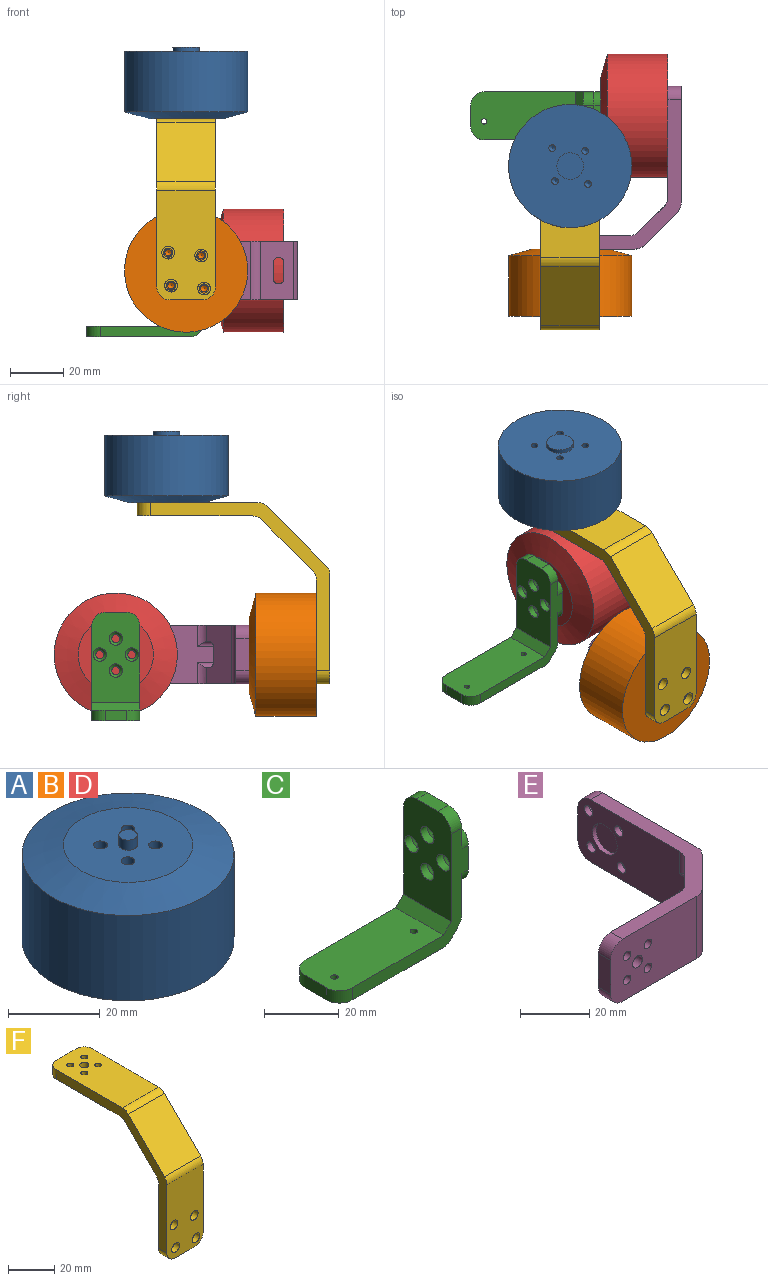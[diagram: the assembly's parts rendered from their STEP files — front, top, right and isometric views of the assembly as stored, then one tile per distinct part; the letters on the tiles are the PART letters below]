
ASSEMBLY  parts=6 mates=5
PART A: 24 faces, bbox 46.2x46.2x29.5 mm
  f0: cylinder r=23.1mm len=46.2mm, axis (0,0,-1), area 3302mm2, adj f2,f21
  f1: plane 28.2x28.2mm, normal (0,0,1), area 583.7mm2, adj f4,f6,f8,f10,f19,f21
  f2: plane 46.2x46.2mm, normal (0,0,-1), area 1578.2mm2, adj f0,f12,f14,f16,f18,f22
  f3: cone r=0mm half-angle=59deg, axis (0,0,1), area 8.2mm2, adj f4
  f4: cylinder r=1.5mm len=7mm, axis (0,0,1), area 66mm2, adj f1,f3
  f5: cone r=0mm half-angle=59deg, axis (0,0,1), area 8.2mm2, adj f6
  f6: cylinder r=1.5mm len=7mm, axis (0,0,1), area 66mm2, adj f1,f5
  f7: cone r=0mm half-angle=59deg, axis (0,0,1), area 8.2mm2, adj f8
  f8: cylinder r=1.5mm len=7mm, axis (0,0,1), area 66mm2, adj f1,f7
  f9: cone r=0mm half-angle=59deg, axis (0,0,1), area 8.2mm2, adj f10
  f10: cylinder r=1.5mm len=7mm, axis (0,0,1), area 66mm2, adj f1,f9
  f11: cone r=0mm half-angle=59deg, axis (0,0,-1), area 5.7mm2, adj f12
  f12: cylinder r=1.25mm len=7mm, axis (0,0,-1), area 55mm2, adj f2,f11
  f13: cone r=0mm half-angle=59deg, axis (0,0,-1), area 5.7mm2, adj f14
  f14: cylinder r=1.25mm len=7mm, axis (0,0,-1), area 55mm2, adj f2,f13
  f15: cone r=0mm half-angle=59deg, axis (0,0,-1), area 5.7mm2, adj f16
  f16: cylinder r=1.25mm len=7mm, axis (0,0,-1), area 55mm2, adj f2,f15
  f17: cone r=0mm half-angle=59deg, axis (0,0,-1), area 5.7mm2, adj f18
  f18: cylinder r=1.25mm len=7mm, axis (0,0,-1), area 55mm2, adj f2,f17
  f19: cylinder r=2mm len=4mm, axis (0,0,-1), area 33.9mm2, adj f1,f20
  f20: plane 4x4mm, normal (0,0,1), area 12.6mm2, adj f19
  f21: cone r=14.1mm half-angle=74.5deg, axis (0,0,-1), area 1091.6mm2, adj f0,f1
  f22: cylinder r=5mm len=10mm, axis (0,0,1), area 47.1mm2, adj f2,f23
  f23: plane 10x10mm, normal (0,0,-1), area 78.5mm2, adj f22
PART B: same geometry as A
PART C: 48 faces, bbox 48.7x18x40.6 mm
  f0: plane 18x11.82mm, normal (1,0,0), area 122.8mm2, adj f7,f9,f10,f11,f38,f41,f44,f46
  f1: plane 18x2.97mm, normal (-0.71,0,0.71), area 75.6mm2, adj f2,f8,f9,f10
  f2: plane 39.26x18mm, normal (0,0,1), area 689.6mm2, adj f1,f3,f9,f10,f14,f17,f45,f47
  f3: plane 8x4mm, normal (-1,0,0), area 32mm2, adj f2,f4,f45,f47
  f4: plane 38.84x18mm, normal (0,0,-1), area 653.8mm2, adj f3,f9,f10,f16,f19,f35,f37,f42
  f5: plane 18x2.38mm, normal (0.71,0,-0.71), area 60.7mm2, adj f9,f10,f42,f43
  f6: plane 18x13.42mm, normal (1,0,0), area 162.2mm2, adj f9,f10,f12,f39,f40,f43
  f7: plane 8x4mm, normal (0,0,1), area 32mm2, adj f0,f8,f44,f46
  f8: plane 33.65x18mm, normal (-1,0,0), area 516.4mm2, adj f1,f7,f9,f10,f21,f23,f25,f27
  f9: plane 43.73x35.62mm, normal (0,1,0), area 300.6mm2, adj f0,f1,f2,f4,f5,f6,f8,f13
  f10: plane 43.73x35.62mm, normal (0,-1,0), area 300.6mm2, adj f0,f1,f2,f4,f5,f6,f8,f13
  f11: plane 8x2.5mm, normal (0,0,1), area 20mm2, adj f0,f13,f38,f41
  f12: plane 8x2.5mm, normal (0,0,-1), area 20mm2, adj f6,f13,f39,f40
  f13: plane 18x18mm, normal (1,0,0), area 261.7mm2, adj f9,f10,f11,f12,f20,f22,f24,f26
  f14: cylinder r=1mm len=2mm, axis (0,0,-1), area 12.6mm2, adj f2,f15
  f15: plane 4x4mm, normal (0,0,-1), area 9.4mm2, adj f14,f16
  f16: cylinder r=2mm len=4mm, axis (0,0,-1), area 25.1mm2, adj f4,f15
  f17: cylinder r=1mm len=2mm, axis (0,0,-1), area 12.6mm2, adj f2,f18
  f18: plane 4x4mm, normal (0,0,-1), area 9.4mm2, adj f17,f19
  f19: cylinder r=2mm len=4mm, axis (0,0,-1), area 25.1mm2, adj f4,f18
  f20: cylinder r=1.5mm len=3mm, axis (-1,0,0), area 28.3mm2, adj f13,f29
  f21: cylinder r=2.5mm len=5mm, axis (-1,0,0), area 39.3mm2, adj f8,f29
  f22: cylinder r=1.5mm len=3mm, axis (-1,0,0), area 28.3mm2, adj f13,f28
  f23: cylinder r=2.5mm len=5mm, axis (-1,0,0), area 39.3mm2, adj f8,f28
  f24: cylinder r=1.5mm len=3mm, axis (-1,0,0), area 28.3mm2, adj f13,f30
  f25: cylinder r=2.5mm len=5mm, axis (-1,0,0), area 39.3mm2, adj f8,f30
  f26: cylinder r=1.5mm len=3mm, axis (-1,0,0), area 28.3mm2, adj f13,f31
  f27: cylinder r=2.5mm len=5mm, axis (-1,0,0), area 39.3mm2, adj f8,f31
  f28: cone r=1.5mm half-angle=45deg, axis (-1,0,0), area 17.8mm2, adj f22,f23
  f29: cone r=1.5mm half-angle=45deg, axis (-1,0,0), area 17.8mm2, adj f20,f21
  f30: cone r=1.5mm half-angle=45deg, axis (-1,0,0), area 17.8mm2, adj f24,f25
  f31: cone r=1.5mm half-angle=45deg, axis (-1,0,0), area 17.8mm2, adj f26,f27
  f32: cylinder r=2mm len=4mm, axis (1,0,0), area 37.7mm2, adj f13,f33
  f33: plane 4x4mm, normal (1,0,0), area 12.6mm2, adj f32
  f34: cone r=0mm half-angle=59deg, axis (0,0,-1), area 5.5mm2, adj f35
  f35: cylinder r=1.22mm len=2.5mm, axis (0,0,-1), area 19.2mm2, adj f4,f34
  f36: cone r=0mm half-angle=59deg, axis (0,0,-1), area 5.5mm2, adj f37
  f37: cylinder r=1.22mm len=2.5mm, axis (0,0,-1), area 19.2mm2, adj f4,f36
  f38: cylinder r=5mm len=5mm, axis (1,0,0), area 19.6mm2, adj f0,f9,f11,f13
  f39: cylinder r=5mm len=5mm, axis (-1,0,0), area 19.6mm2, adj f6,f9,f12,f13
  f40: cylinder r=5mm len=5mm, axis (1,0,0), area 19.6mm2, adj f6,f10,f12,f13
  f41: cylinder r=5mm len=5mm, axis (-1,0,0), area 19.6mm2, adj f0,f10,f11,f13
  f42: cylinder r=5mm len=18mm, axis (0,-1,0), area 70.7mm2, adj f4,f5,f9,f10
  f43: cylinder r=5mm len=18mm, axis (0,-1,0), area 70.7mm2, adj f5,f6,f9,f10
  f44: cylinder r=5mm len=5mm, axis (-1,0,0), area 31.4mm2, adj f0,f7,f8,f10
  f45: cylinder r=5mm len=5mm, axis (0,0,-1), area 31.4mm2, adj f2,f3,f4,f10
  f46: cylinder r=5mm len=5mm, axis (1,0,0), area 31.4mm2, adj f0,f7,f8,f9
  f47: cylinder r=5mm len=5mm, axis (0,0,1), area 31.4mm2, adj f2,f3,f4,f9
PART D: same geometry as A
PART E: 50 faces, bbox 52.7x61x22 mm
  f0: plane 33.23x22mm, normal (0,1,0), area 641.7mm2, adj f1,f8,f9,f23,f25,f27,f29,f45
  f1: plane 12x5mm, normal (-1,0,0), area 60mm2, adj f0,f2,f47,f49
  f2: plane 35.3x22mm, normal (0,-1,0), area 724.9mm2, adj f1,f8,f9,f22,f24,f26,f28,f36
  f3: plane 22x12.39mm, normal (0.71,-0.71,0), area 333.9mm2, adj f6,f8,f9,f38,f39,f40,f42,f43
  f4: plane 43.61x22mm, normal (1,0,0), area 877.7mm2, adj f5,f8,f9,f12,f15,f18,f21,f43
  f5: plane 12x5mm, normal (0,1,0), area 60mm2, adj f4,f6,f46,f48
  f6: plane 50.68x22mm, normal (-1,0,0), area 843mm2, adj f3,f5,f8,f9,f10,f13,f16,f19
  f7: plane 22x9.47mm, normal (-0.71,0.71,0), area 261.1mm2, adj f8,f9,f38,f39,f40,f41,f44,f45
  f8: plane 56x47.69mm, normal (0,0,1), area 452.9mm2, adj f0,f2,f3,f4,f6,f7,f42,f43
  f9: plane 56x47.69mm, normal (0,0,-1), area 452.9mm2, adj f0,f2,f3,f4,f6,f7,f41,f42
  f10: cylinder r=1.7mm len=3.4mm, axis (1,0,0), area 21.4mm2, adj f6,f11
  f11: plane 4.75x4.75mm, normal (1,0,0), area 8.6mm2, adj f10,f12
  f12: cylinder r=2.38mm len=4.75mm, axis (1,0,0), area 44.8mm2, adj f4,f11
  f13: cylinder r=1.7mm len=3.4mm, axis (1,0,0), area 21.4mm2, adj f6,f14
  f14: plane 4.75x4.75mm, normal (1,0,0), area 8.6mm2, adj f13,f15
  f15: cylinder r=2.38mm len=4.75mm, axis (1,0,0), area 44.8mm2, adj f4,f14
  f16: cylinder r=1.7mm len=3.4mm, axis (1,0,0), area 21.4mm2, adj f6,f17
  f17: plane 4.75x4.75mm, normal (1,0,0), area 8.6mm2, adj f16,f18
  f18: cylinder r=2.38mm len=4.75mm, axis (1,0,0), area 44.8mm2, adj f4,f17
  f19: cylinder r=1.7mm len=3.4mm, axis (1,0,0), area 21.4mm2, adj f6,f20
  f20: plane 4.75x4.75mm, normal (1,0,0), area 8.6mm2, adj f19,f21
  f21: cylinder r=2.38mm len=4.75mm, axis (1,0,0), area 44.8mm2, adj f4,f20
  f22: cylinder r=1.5mm len=3mm, axis (0,1,0), area 28.3mm2, adj f2,f32
  f23: cylinder r=2.5mm len=5mm, axis (0,1,0), area 15.7mm2, adj f0,f32
  f24: cylinder r=1.5mm len=3mm, axis (0,1,0), area 28.3mm2, adj f2,f31
  f25: cylinder r=2.5mm len=5mm, axis (0,1,0), area 15.7mm2, adj f0,f31
  f26: cylinder r=1.5mm len=3mm, axis (0,1,0), area 28.3mm2, adj f2,f30
  f27: cylinder r=2.5mm len=5mm, axis (0,1,0), area 15.7mm2, adj f0,f30
  f28: cylinder r=1.5mm len=3mm, axis (0,1,0), area 28.3mm2, adj f2,f33
  f29: cylinder r=2.5mm len=5mm, axis (0,1,0), area 15.7mm2, adj f0,f33
  f30: cone r=1.5mm half-angle=45deg, axis (0,1,0), area 17.8mm2, adj f26,f27
  f31: cone r=1.5mm half-angle=45deg, axis (0,1,0), area 17.8mm2, adj f24,f25
  f32: cone r=1.5mm half-angle=45deg, axis (0,1,0), area 17.8mm2, adj f22,f23
  f33: cone r=1.5mm half-angle=45deg, axis (0,1,0), area 17.8mm2, adj f28,f29
  f34: cylinder r=5mm len=10mm, axis (-1,0,0), area 47.1mm2, adj f6,f35
  f35: plane 10x10mm, normal (-1,0,0), area 78.5mm2, adj f34
  f36: cylinder r=2mm len=4mm, axis (0,-1,0), area 37.7mm2, adj f2,f37
  f37: plane 4x4mm, normal (0,-1,0), area 12.6mm2, adj f36
  f38: plane 7.07x6mm, normal (1,0,0), area 42.4mm2, adj f3,f7,f39,f40
  f39: cylinder r=2mm len=13.14mm, axis (0,1,0), area 46.2mm2, adj f3,f6,f7,f38,f44
  f40: cylinder r=2mm len=13.14mm, axis (0,1,0), area 46.2mm2, adj f3,f6,f7,f38,f41
  f41: cylinder r=5mm len=8mm, axis (0,0,1), area 27.1mm2, adj f6,f7,f9,f40
  f42: cylinder r=5mm len=22mm, axis (0,0,-1), area 86.4mm2, adj f2,f3,f8,f9
  f43: cylinder r=5mm len=22mm, axis (0,0,-1), area 86.4mm2, adj f3,f4,f8,f9
  f44: cylinder r=5mm len=8mm, axis (0,0,1), area 27.1mm2, adj f6,f7,f8,f39
  f45: cylinder r=5mm len=22mm, axis (0,0,1), area 86.4mm2, adj f0,f7,f8,f9
  f46: cylinder r=5mm len=5mm, axis (-1,0,0), area 39.3mm2, adj f4,f5,f6,f9
  f47: cylinder r=5mm len=5mm, axis (0,-1,0), area 39.3mm2, adj f0,f1,f2,f9
  f48: cylinder r=5mm len=5mm, axis (1,0,0), area 39.3mm2, adj f4,f5,f6,f8
  f49: cylinder r=5mm len=5mm, axis (0,1,0), area 39.3mm2, adj f0,f1,f2,f8
PART F: 46 faces, bbox 22x72.3x68 mm
  f0: plane 41x22mm, normal (0,-1,0), area 820.4mm2, adj f1,f8,f9,f14,f17,f20,f23,f41
  f1: plane 12x5mm, normal (0,0,-1), area 60mm2, adj f0,f2,f43,f45
  f2: plane 38.93x22mm, normal (0,1,0), area 730.8mm2, adj f1,f8,f9,f10,f12,f15,f18,f21
  f3: plane 22x19.07mm, normal (0,0.71,-0.71), area 593.4mm2, adj f8,f9,f38,f39
  f4: plane 43.18x22mm, normal (0,0,-1), area 860.7mm2, adj f5,f8,f9,f25,f27,f29,f31,f39
  f5: plane 12x5mm, normal (0,1,0), area 60mm2, adj f4,f6,f42,f44
  f6: plane 45.25x22mm, normal (0,0,1), area 943.9mm2, adj f5,f8,f9,f24,f26,f28,f30,f36
  f7: plane 22x22mm, normal (0,-0.71,0.71), area 684.5mm2, adj f8,f9,f40,f41
  f8: plane 67.25x63mm, normal (1,0,0), area 557.5mm2, adj f0,f2,f3,f4,f6,f7,f38,f39
  f9: plane 67.25x63mm, normal (-1,0,0), area 557.5mm2, adj f0,f2,f3,f4,f6,f7,f38,f39
  f10: cylinder r=5mm len=10mm, axis (0,1,0), area 47.1mm2, adj f2,f11
  f11: plane 10x10mm, normal (0,1,0), area 78.5mm2, adj f10
  f12: cylinder r=1.7mm len=3.4mm, axis (0,-1,0), area 21.4mm2, adj f2,f13
  f13: plane 4.75x4.75mm, normal (0,-1,0), area 8.6mm2, adj f12,f14
  f14: cylinder r=2.38mm len=4.75mm, axis (0,-1,0), area 44.8mm2, adj f0,f13
  f15: cylinder r=1.7mm len=3.4mm, axis (0,-1,0), area 21.4mm2, adj f2,f16
  f16: plane 4.75x4.75mm, normal (0,-1,0), area 8.6mm2, adj f15,f17
  f17: cylinder r=2.38mm len=4.75mm, axis (0,-1,0), area 44.8mm2, adj f0,f16
  f18: cylinder r=1.7mm len=3.4mm, axis (0,-1,0), area 21.4mm2, adj f2,f19
  f19: plane 4.75x4.75mm, normal (0,-1,0), area 8.6mm2, adj f18,f20
  f20: cylinder r=2.38mm len=4.75mm, axis (0,-1,0), area 44.8mm2, adj f0,f19
  f21: cylinder r=1.7mm len=3.4mm, axis (0,-1,0), area 21.4mm2, adj f2,f22
  f22: plane 4.75x4.75mm, normal (0,-1,0), area 8.6mm2, adj f21,f23
  f23: cylinder r=2.38mm len=4.75mm, axis (0,-1,0), area 44.8mm2, adj f0,f22
  f24: cylinder r=1.5mm len=3mm, axis (0,0,-1), area 28.3mm2, adj f6,f35
  f25: cylinder r=2.5mm len=5mm, axis (0,0,-1), area 15.7mm2, adj f4,f35
  f26: cylinder r=1.5mm len=3mm, axis (0,0,-1), area 28.3mm2, adj f6,f34
  f27: cylinder r=2.5mm len=5mm, axis (0,0,-1), area 15.7mm2, adj f4,f34
  f28: cylinder r=1.5mm len=3mm, axis (0,0,-1), area 28.3mm2, adj f6,f33
  f29: cylinder r=2.5mm len=5mm, axis (0,0,-1), area 15.7mm2, adj f4,f33
  f30: cylinder r=1.5mm len=3mm, axis (0,0,-1), area 28.3mm2, adj f6,f32
  f31: cylinder r=2.5mm len=5mm, axis (0,0,-1), area 15.7mm2, adj f4,f32
  f32: cone r=1.5mm half-angle=45deg, axis (0,0,-1), area 17.8mm2, adj f30,f31
  f33: cone r=1.5mm half-angle=45deg, axis (0,0,-1), area 17.8mm2, adj f28,f29
  f34: cone r=1.5mm half-angle=45deg, axis (0,0,-1), area 17.8mm2, adj f26,f27
  f35: cone r=1.5mm half-angle=45deg, axis (0,0,-1), area 17.8mm2, adj f24,f25
  f36: cylinder r=2mm len=4mm, axis (0,0,1), area 37.7mm2, adj f6,f37
  f37: plane 4x4mm, normal (0,0,1), area 12.6mm2, adj f36
  f38: cylinder r=5mm len=22mm, axis (1,0,0), area 86.4mm2, adj f2,f3,f8,f9
  f39: cylinder r=5mm len=22mm, axis (1,0,0), area 86.4mm2, adj f3,f4,f8,f9
  f40: cylinder r=5mm len=22mm, axis (-1,0,0), area 86.4mm2, adj f6,f7,f8,f9
  f41: cylinder r=5mm len=22mm, axis (-1,0,0), area 86.4mm2, adj f0,f7,f8,f9
  f42: cylinder r=5mm len=5mm, axis (0,0,1), area 39.3mm2, adj f4,f5,f6,f9
  f43: cylinder r=5mm len=5mm, axis (0,1,0), area 39.3mm2, adj f0,f1,f2,f9
  f44: cylinder r=5mm len=5mm, axis (0,0,-1), area 39.3mm2, adj f4,f5,f6,f8
  f45: cylinder r=5mm len=5mm, axis (0,-1,0), area 39.3mm2, adj f0,f1,f2,f8
PLACE A rot(axis=(1,0,0),180deg) t=(0,0,-1.5)mm
PLACE B rot(axis=(-1,0,0),90deg) t=(0,-56.25,-83.75)mm
PLACE C t=(-0.25,19,-83.75)mm
PLACE D rot(axis=(0,-1,0),90deg) t=(36.69,19,-83.75)mm
PLACE E t=(0,0.25,-83.75)mm
PLACE F t=(0,0,-83.75)mm
MATE fastened E.f34 <-> D.f0  axis (-1,0,0) through (36.69,19,-83.75)mm
MATE revolute C.f32 <-> D.f0  axis (1,0,0) through (11.44,19,-83.75)mm
MATE fastened B.f0 <-> F.f10  axis (0,-1,0) through (0,-56.25,-83.75)mm
MATE revolute A.f0 <-> F.f36  axis (0,0,-1) through (0,0,-26.75)mm
MATE revolute B.f19 <-> E.f36  axis (0,1,0) through (0,-31,-83.75)mm
